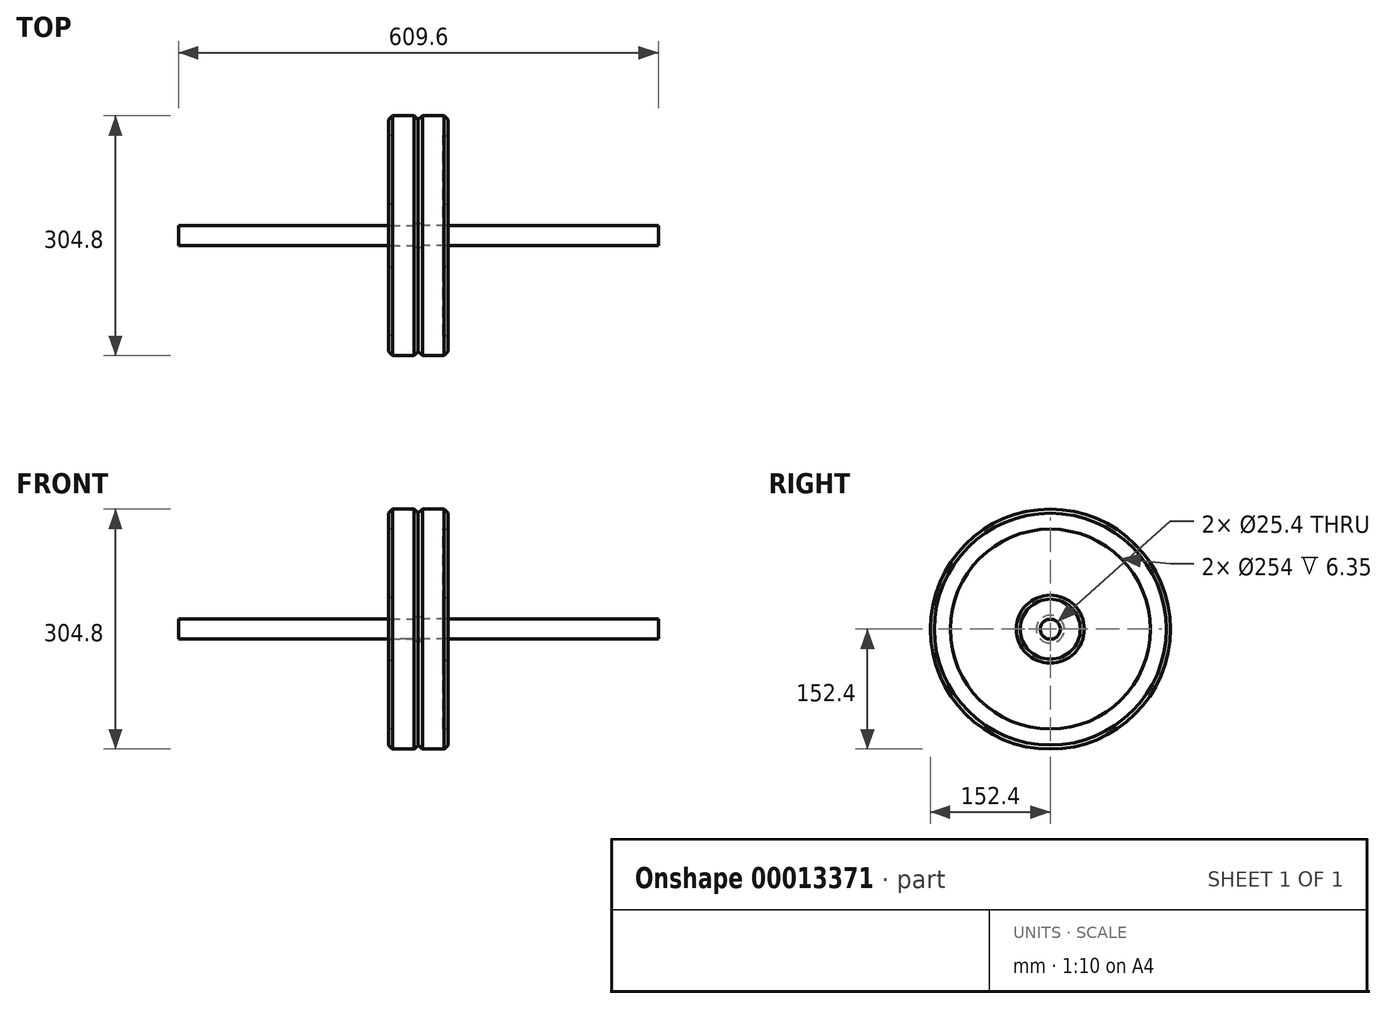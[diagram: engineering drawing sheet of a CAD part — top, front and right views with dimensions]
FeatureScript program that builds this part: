
annotation { "Feature Type Name" : "Feature", "Feature Type Description" : "" }
export const myFeature = defineFeature(function(context is Context, id is Id, definition is map)
    precondition{}
    {
        {
            var Q0;
            Q0=qCreatedBy(makeId("Right.planeOp"),FACE);
            var sketch = newSketch(context, id + "F0", { "sketchPlane" : qUnion([Q0])});
            skCircle(sketch, "E0", {"center": v(0, 0) * mm, "radius": 12.7 * mm});
            skSolve(sketch);
        }
        {
            var Q0;
            Q0=qSketchRegion(id+"F0",true);
            extrude(context, id + "F1", {"entities" : qUnion([Q0]), "depth" : 304.8 * mm, "hasSecondDirection" : true, "secondDirectionOppositeDirection" : true, "secondDirectionDepth" : 304.8 * mm});
        }
        {
            var Q0;
            Q0=qCreatedBy(makeId("Right.planeOp"),FACE);
            var sketch = newSketch(context, id + "F2", { "sketchPlane" : qUnion([Q0])});
            skCircle(sketch, "E1", {"center": v(0, 0) * mm, "radius": 152.4 * mm});
            skCircle(sketch, "E2", {"center": v(0, 0) * mm, "radius": 12.7 * mm});
            skSolve(sketch);
        }
        {
            var Q0;
            Q0=qSketchRegion(id+"F2",true);
            extrude(context, id + "F3", {"entities" : qUnion([Q0]), "depth" : 38.1 * mm});
        }
        {
            var Q0;
            Q0=makeQuery(id+"F3.opExtrude","CAP_FACE",FACE,{"disambiguationData":[OSD([sQuery(id+"F2.wireOp",EDGE,"E1"),sQuery(id+"F2.wireOp",EDGE,"E2")])],"isStart":false});
            var sketch = newSketch(context, id + "F4", { "sketchPlane" : qUnion([Q0])});
            skCircle(sketch, "E3.0", {"center": v(0, 0) * mm, "radius": 127 * mm});
            skCircle(sketch, "E4.0", {"center": v(0, 0) * mm, "radius": 38.1 * mm});
            skSolve(sketch);
        }
        {
            var Q0;
            Q0=makeQuery(id+"F4.imprint","IMPRINT",FACE,{"disambiguationData":[TD([[makeQuery(id+"F4.imprint","IMPRINT",EDGE,{"derivedFrom":sQuery(id+"F4.wireOp",EDGE,"E3.0")}),1.0]])]});
            extrude(context, id + "F5", {"entities" : qUnion([Q0]), "operationType" : NewBodyOperationType.REMOVE, "oppositeDirection" : true, "depth" : 6.35 * mm});
        }
        {
            var Q0;
            Q0=makeQuery(id+"F5.boolean.opBoolean","COPY",EDGE,{"derivedFrom":makeQuery(id+"F5.opExtrude","CAP_EDGE",EDGE,{"disambiguationData":[OSD([sQuery(id+"F4.wireOp",EDGE,"E3.0")])],"isStart":true})});
            var Q1;
            Q1=makeQuery(id+"F5.boolean.opBoolean","COPY",EDGE,{"derivedFrom":makeQuery(id+"F5.opExtrude","CAP_EDGE",EDGE,{"disambiguationData":[OSD([sQuery(id+"F4.wireOp",EDGE,"E4.0")])],"isStart":false})});
            var Q2;
            Q2=makeQuery(id+"F3.opExtrude","CAP_EDGE",EDGE,{"disambiguationData":[OSD([sQuery(id+"F2.wireOp",EDGE,"E1")])],"isStart":false});
            var Q3;
            Q3=makeQuery(id+"F3.opExtrude","CAP_FACE",FACE,{"disambiguationData":[OSD([sQuery(id+"F2.wireOp",EDGE,"E1"),sQuery(id+"F2.wireOp",EDGE,"E2")])],"isStart":true});
            chamfer(context, id + "F6", {"entities" : qUnion([Q0, Q1, Q2, Q3]), "width" : 5.08 * mm, "tangentPropagation" : true});
        }
        {
            var Q0;
            Q0=makeQuery(id+"F3.opExtrude","SWEPT_BODY",BODY,{"disambiguationData":[OSD([sQuery(id+"F2.wireOp",EDGE,"E1"),sQuery(id+"F2.wireOp",EDGE,"E2")])]});
            var Q1;
            Q1=makeQuery(id+"F3.opExtrude","CAP_FACE",FACE,{"disambiguationData":[OSD([sQuery(id+"F2.wireOp",EDGE,"E1"),sQuery(id+"F2.wireOp",EDGE,"E2")])],"isStart":true});
            mirror(context, id + "F7", {"entities" : qUnion([Q0]), "mirrorPlane" : qUnion([Q1])});
        }
    });
